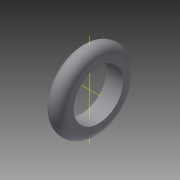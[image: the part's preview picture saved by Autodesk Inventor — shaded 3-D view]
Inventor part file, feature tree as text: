
AUTODESK INVENTOR PART (.ipt)
format: ipt  version: 2015 (Build 190159000, 159)  size: 110,080 bytes
history: native  units: mm
features: revolve x1, fillet x1, sketch x1
ambient origin geometry x8: Origin, YZ Plane, XZ Plane, XY Plane, X Axis, Y Axis, Z Axis, Center Point
bodies: Solid1 (feature_tree)
feature tree (3):
  revolve  "Revolution1"  [1 undecoded]
  fillet  "Fillet1"  Radius=55.0mm
  sketch  "Sketch1"  dims[d1=24.0mm d2=35.0mm d3=55.0mm d4=90.0deg d5=12.0mm]
note: 1 required parameter value undecoded (feature->parameter linkage not recoverable at this tier; creation-order binding heuristic only, values carry confidence <= 0.55)
